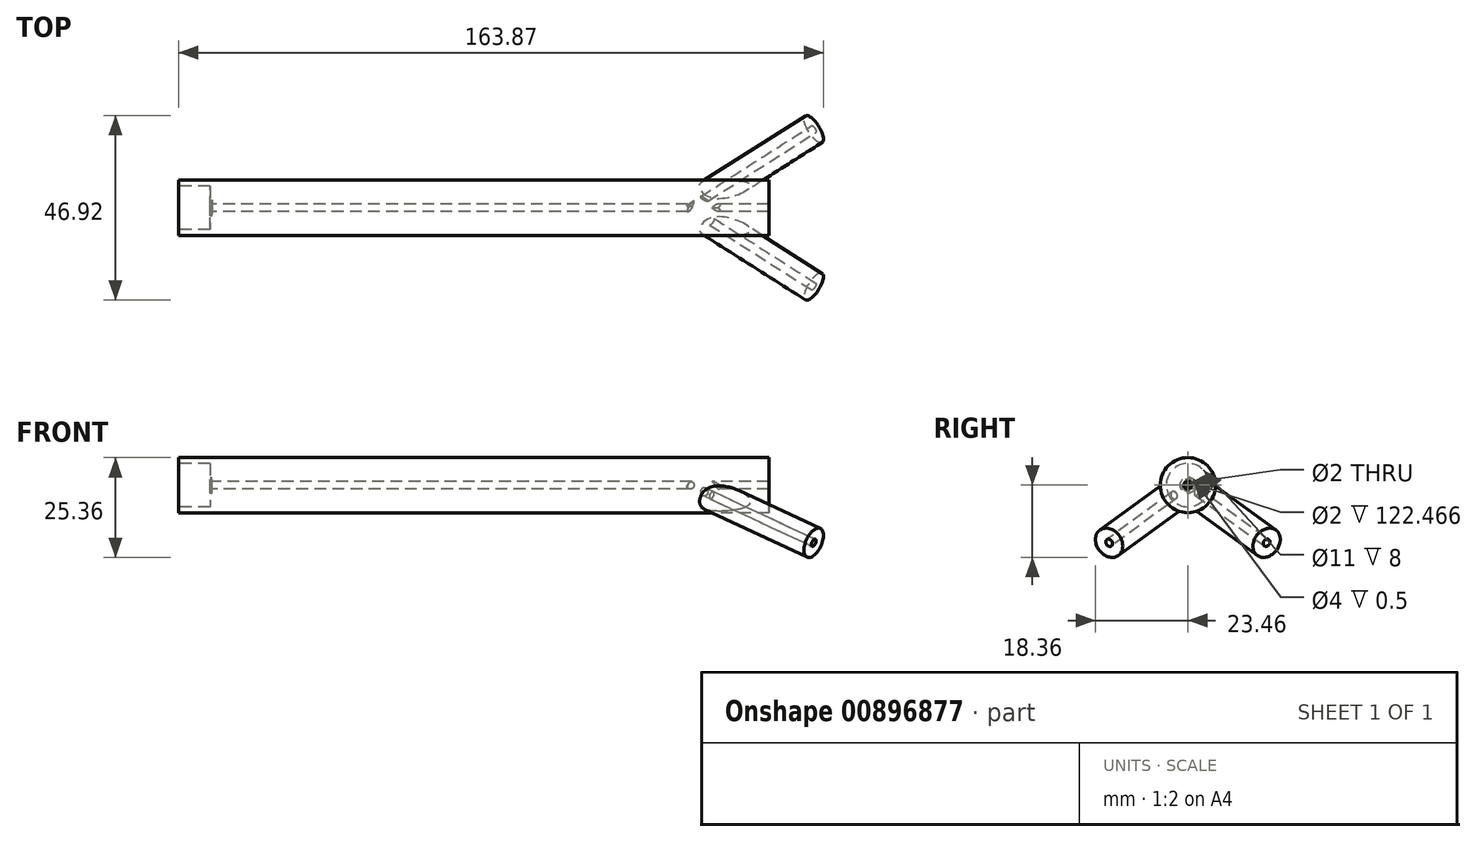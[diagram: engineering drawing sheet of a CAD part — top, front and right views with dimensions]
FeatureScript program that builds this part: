
annotation { "Feature Type Name" : "Feature", "Feature Type Description" : "" }
export const myFeature = defineFeature(function(context is Context, id is Id, definition is map)
    precondition{}
    {
        {
            var Q0;
            Q0=qCreatedBy(makeId("Right.planeOp"),FACE);
            var sketch = newSketch(context, id + "F0", { "sketchPlane" : qUnion([Q0])});
            skCircle(sketch, "E0", {"center": v(0, 0) * mm, "radius": 7 * mm});
            skSolve(sketch);
        }
        {
            var Q0;
            Q0=makeQuery(id+"F0.imprint","IMPRINT",FACE,{"disambiguationData":[TD([[makeQuery(id+"F0.imprint","IMPRINT",EDGE,{"derivedFrom":sQuery(id+"F0.wireOp",EDGE,"E0")}),1.0]])]});
            extrude(context, id + "F1", {"entities" : qUnion([Q0]), "endBound" : BoundingType.SYMMETRIC, "depth" : 150 * mm, "offsetDistance" : 25.4 * mm});
        }
        {
            var Q0;
            Q0=makeQuery(id+"F1.opExtrude","CAP_FACE",FACE,{"disambiguationData":[OSD([sQuery(id+"F0.wireOp",EDGE,"E0")])],"isStart":true});
            var sketch = newSketch(context, id + "F2", { "sketchPlane" : qUnion([Q0])});
            skCircle(sketch, "E1", {"center": v(0, 0) * mm, "radius": 1 * mm});
            skSolve(sketch);
        }
        {
            var Q0;
            Q0 = qSketchRegion(id + "F2", true);
            extrude(context, id + "F3", {"entities" : qUnion([Q0]), "operationType" : NewBodyOperationType.REMOVE, "endBound" : BoundingType.THROUGH_ALL, "oppositeDirection" : true, "depth" : 25.4 * mm, "offsetDistance" : 25.4 * mm});
        }
        {
            var Q0;
            Q0=makeQuery(id+"F1.opExtrude","CAP_FACE",FACE,{"disambiguationData":[OSD([sQuery(id+"F0.wireOp",EDGE,"E0")])],"isStart":true});
            var sketch = newSketch(context, id + "F4", { "sketchPlane" : qUnion([Q0])});
            skCircle(sketch, "E2", {"center": v(0, 0) * mm, "radius": 5.5 * mm});
            skSolve(sketch);
        }
        {
            var Q0;
            Q0=makeQuery(id+"F4.imprint","IMPRINT",FACE,{"disambiguationData":[TD([[makeQuery(id+"F4.imprint","IMPRINT",EDGE,{"derivedFrom":sQuery(id+"F4.wireOp",EDGE,"E2")}),1.0]])]});
            extrude(context, id + "F5", {"entities" : qUnion([Q0]), "operationType" : NewBodyOperationType.REMOVE, "oppositeDirection" : true, "depth" : 8 * mm, "offsetDistance" : 25.4 * mm});
        }
        {
            var Q0;
            Q0=qCreatedBy(makeId("Top.planeOp"),FACE);
            var sketch = newSketch(context, id + "F6", { "sketchPlane" : qUnion([Q0])});
            skLineSegment(sketch, "E3.0", {"start": v(-67, -1) * mm, "end": v(-67, 1) * mm});
            skLineSegment(sketch, "E4.bottom", {"start": v(-67, 1.5) * mm, "end": v(-66.5, 1.5) * mm});
            skLineSegment(sketch, "E4.top", {"start": v(-67, 2) * mm, "end": v(-66.5, 2) * mm});
            skLineSegment(sketch, "E4.left", {"start": v(-67, 1.5) * mm, "end": v(-67, 2) * mm});
            skLineSegment(sketch, "E4.right", {"start": v(-66.5, 1.5) * mm, "end": v(-66.5, 2) * mm});
            skLineSegment(sketch, "E5", {"start": v(-67.9, 0) * mm, "end": v(-52.62, 0) * mm});
            skSolve(sketch);
        }
        {
            var Q0;
            Q0 = qSketchRegion(id + "F6", true);
            var Q1;
            Q1=sQuery(id+"F6.wireOp",EDGE,"E5");
            revolve(context, id + "F7", {"operationType" : NewBodyOperationType.REMOVE, "surfaceOperationType" : NewSurfaceOperationType.NEW, "entities" : qUnion([Q0]), "axis" : qUnion([Q1]), "revolveType" : RevolveType.FULL, "oppositeDirection" : true});
        }
        {
            var Q0;
            Q0=makeQuery(id+"F1.opExtrude","CAP_FACE",FACE,{"disambiguationData":[OSD([sQuery(id+"F0.wireOp",EDGE,"E0")])],"isStart":false});
            cPlane(context, id + "F8", {"entities" : qUnion([Q0]), "cplaneType" : CPlaneType.OFFSET, "offset" : 20 * mm, "oppositeDirection" : true, "width" : 152.4 * mm, "height" : 152.4 * mm});
        }
        {
            var Q0;
            Q0=qCreatedBy(id+"F8.planeOp",FACE);
            var sketch = newSketch(context, id + "F9", { "sketchPlane" : qUnion([Q0])});
            skPoint(sketch, "E6.0", {"position": v(0, 0) * mm});
            skLineSegment(sketch, "E7", {"start": v(7.86, 0) * mm, "end": v(-18.1, 0) * mm});
            skSolve(sketch);
        }
        {
            var Q0;
            Q0=qCreatedBy(id+"F8.planeOp",FACE);
            var Q1;
            Q1=sQuery(id+"F9.wireOp",EDGE,"E7");
            cPlane(context, id + "F10", {"entities" : qUnion([Q0, Q1]), "cplaneType" : CPlaneType.LINE_ANGLE, "offset" : 25.4 * mm, "angle" : 25 * degree, "oppositeDirection" : true, "width" : 152.4 * mm, "height" : 152.4 * mm});
        }
        {
            var Q0;
            Q0=qCreatedBy(id+"F10.planeOp",FACE);
            var sketch = newSketch(context, id + "F11", { "sketchPlane" : qUnion([Q0])});
            skPoint(sketch, "E8.0", {"position": v(0, 0) * mm});
            skLineSegment(sketch, "E9", {"start": v(0, 20.9) * mm, "end": v(0, -21.68) * mm});
            skSolve(sketch);
        }
        {
            var Q0;
            Q0=qCreatedBy(id+"F10.planeOp",FACE);
            var Q1;
            Q1=sQuery(id+"F11.wireOp",EDGE,"E9");
            cPlane(context, id + "F12", {"entities" : qUnion([Q0, Q1]), "cplaneType" : CPlaneType.LINE_ANGLE, "offset" : 508 * mm, "angle" : 30 * degree, "oppositeDirection" : true, "width" : 152.4 * mm, "height" : 152.4 * mm});
        }
        {
            var Q0;
            Q0=qCreatedBy(id+"F12.planeOp",FACE);
            var sketch = newSketch(context, id + "F13", { "sketchPlane" : qUnion([Q0])});
            skPoint(sketch, "E10.0", {"position": v(0, 0) * mm});
            skPoint(sketch, "E11.0", {"position": v(-24.92, 23.24) * mm});
            skCircle(sketch, "E12", {"center": v(-24.92, 23.24) * mm, "radius": 4 * mm});
            skSolve(sketch);
        }
        {
            var Q0;
            Q0 = qSketchRegion(id + "F13", true);
            extrude(context, id + "F14", {"entities" : qUnion([Q0]), "operationType" : NewBodyOperationType.ADD, "depth" : 40 * mm, "offsetDistance" : 25.4 * mm});
        }
        {
            var Q0;
            Q0=sQuery(id+"F11.wireOp",EDGE,"E9");
            var Q1;
            Q1=qCreatedBy(id+"F12.planeOp",FACE);
            cPlane(context, id + "F15", {"entities" : qUnion([Q0, Q1]), "cplaneType" : CPlaneType.LINE_ANGLE, "offset" : 25.4 * mm, "angle" : 60 * degree, "width" : 152.4 * mm, "height" : 152.4 * mm});
        }
        {
            var Q0;
            Q0=makeQuery(id+"F14.opExtrude","CAP_FACE",FACE,{"disambiguationData":[OSD([sQuery(id+"F13.wireOp",EDGE,"E12")])],"isStart":false});
            var sketch = newSketch(context, id + "F16", { "sketchPlane" : qUnion([Q0])});
            skCircle(sketch, "E13.0", {"center": v(-24.92, 23.24) * mm, "radius": 4 * mm});
            skCircle(sketch, "E14", {"center": v(-24.92, 23.24) * mm, "radius": 1 * mm});
            skSolve(sketch);
        }
        {
            var Q0;
            Q0=makeQuery(id+"F16.imprint","IMPRINT",FACE,{"disambiguationData":[TD([[makeQuery(id+"F16.imprint","IMPRINT",EDGE,{"derivedFrom":sQuery(id+"F16.wireOp",EDGE,"E14")}),1.0]])]});
            extrude(context, id + "F17", {"entities" : qUnion([Q0]), "operationType" : NewBodyOperationType.REMOVE, "oppositeDirection" : true, "depth" : 40 * mm, "offsetDistance" : 25.4 * mm});
        }
        {
            var Q0;
            Q0=qCreatedBy(id+"F15.planeOp",FACE);
            var sketch = newSketch(context, id + "F18", { "sketchPlane" : qUnion([Q0])});
            skPoint(sketch, "E15.0", {"position": v(-24.92, 23.24) * mm});
            skCircle(sketch, "E16", {"center": v(-24.92, 23.24) * mm, "radius": 4 * mm});
            skSolve(sketch);
        }
        {
            var Q0;
            Q0 = qSketchRegion(id + "F18", true);
            extrude(context, id + "F19", {"entities" : qUnion([Q0]), "operationType" : NewBodyOperationType.ADD, "oppositeDirection" : true, "depth" : 40 * mm, "offsetDistance" : 25.4 * mm});
        }
        {
            var Q0;
            Q0=makeQuery(id+"F19.opExtrude","CAP_FACE",FACE,{"disambiguationData":[OSD([sQuery(id+"F18.wireOp",EDGE,"E16")])],"isStart":false});
            var sketch = newSketch(context, id + "F20", { "sketchPlane" : qUnion([Q0])});
            skCircle(sketch, "E17.0.0", {"center": v(24.92, 23.24) * mm, "radius": 4 * mm});
            skCircle(sketch, "E18", {"center": v(24.92, 23.24) * mm, "radius": 1 * mm});
            skSolve(sketch);
        }
        {
            var Q0;
            Q0=makeQuery(id+"F20.imprint","IMPRINT",FACE,{"disambiguationData":[TD([[makeQuery(id+"F20.imprint","IMPRINT",EDGE,{"derivedFrom":sQuery(id+"F20.wireOp",EDGE,"E18")}),1.0]])]});
            extrude(context, id + "F21", {"entities" : qUnion([Q0]), "operationType" : NewBodyOperationType.REMOVE, "oppositeDirection" : true, "depth" : 33 * mm, "offsetDistance" : 25.4 * mm});
        }
    });
